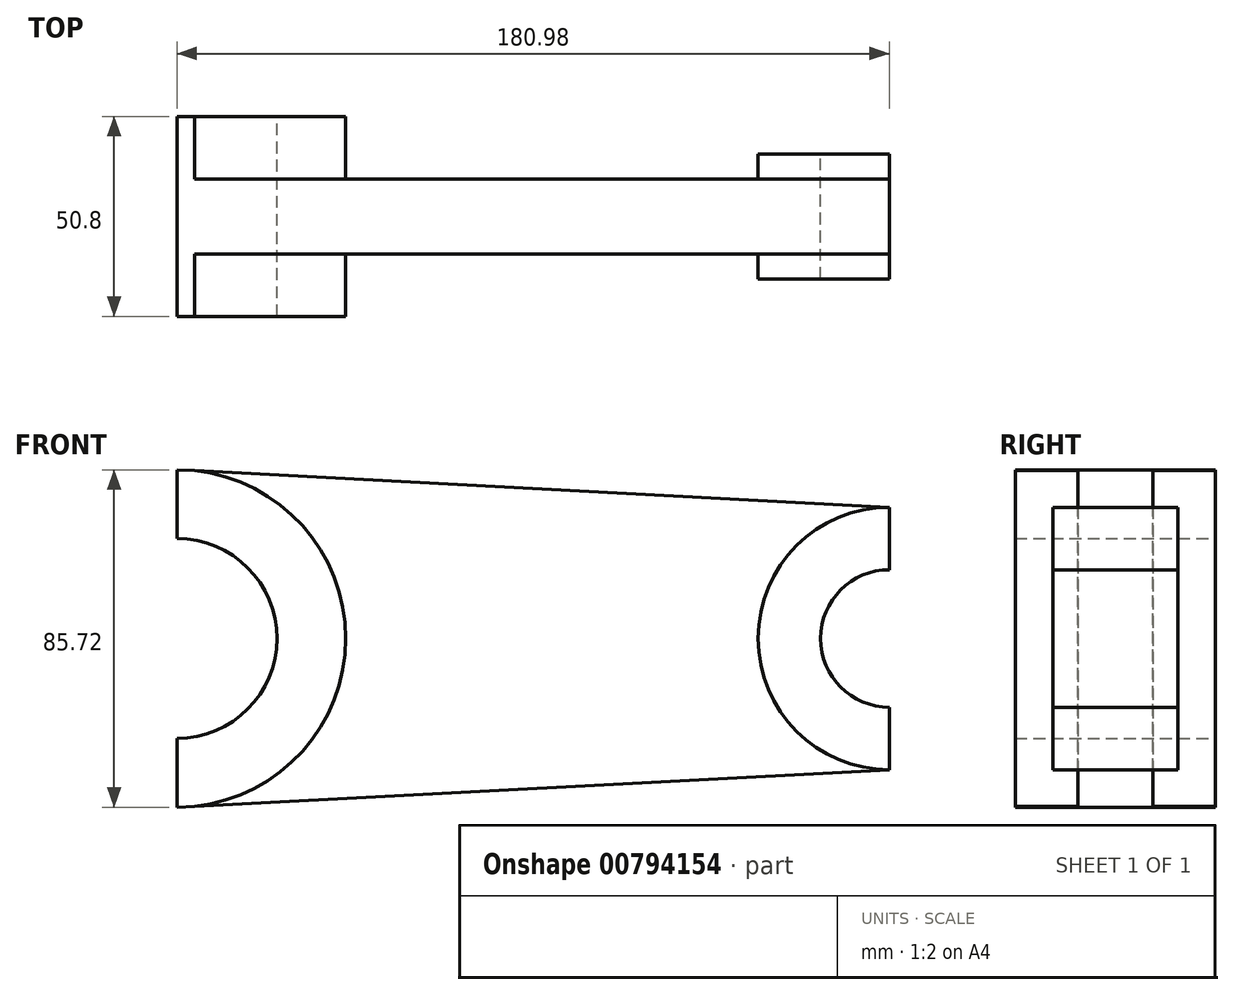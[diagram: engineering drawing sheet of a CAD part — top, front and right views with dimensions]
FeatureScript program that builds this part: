
annotation { "Feature Type Name" : "Feature", "Feature Type Description" : "" }
export const myFeature = defineFeature(function(context is Context, id is Id, definition is map)
    precondition{}
    {
        {
            var Q0;
            Q0=qCreatedBy(makeId("Front.planeOp"),FACE);
            var sketch = newSketch(context, id + "F0", { "sketchPlane" : qUnion([Q0])});
            skCircle(sketch, "E0", {"center": v(0, 0) * mm, "radius": 42.86 * mm});
            skCircle(sketch, "E1", {"center": v(0, 0) * mm, "radius": 25.4 * mm});
            skLineSegment(sketch, "E2", {"start": v(0, 0) * mm, "end": v(180.98, 0) * mm});
            skCircle(sketch, "E3", {"center": v(180.98, 0) * mm, "radius": 33.34 * mm});
            skCircle(sketch, "E4", {"center": v(180.98, 0) * mm, "radius": 17.46 * mm});
            skLineSegment(sketch, "E5", {"start": v(0, 0) * mm, "end": v(0, 42.86) * mm});
            skLineSegment(sketch, "E6", {"start": v(0, 42.86) * mm, "end": v(0, -42.86) * mm});
            skLineSegment(sketch, "E7", {"start": v(180.98, 0) * mm, "end": v(180.98, 33.34) * mm});
            skLineSegment(sketch, "E8", {"start": v(180.98, 33.34) * mm, "end": v(180.98, -33.34) * mm});
            skLineSegment(sketch, "E9", {"start": v(180.97, 33.34) * mm, "end": v(0, 42.86) * mm});
            skLineSegment(sketch, "E10", {"start": v(0, -42.86) * mm, "end": v(180.97, -33.34) * mm});
            skSolve(sketch);
        }
        {
            var Q0;
            {var subQ0=sQuery(id+"F0.wireOp",EDGE,"E9");var subQ2=sQuery(id+"F0.wireOp",EDGE,"E0");var subQ9=makeQuery(id+"F0.imprint","INTERSECT",VERTEX,{"derivedFrom":[subQ2,subQ0]});Q0=makeQuery(id+"F0.imprint","IMPRINT",FACE,{"disambiguationData":[TD([[makeQuery(id+"F0.imprint","IMPRINT",EDGE,{"disambiguationData":[TD([[subQ9,1.0]])],"derivedFrom":subQ2}),1.0]])]});}
            var Q1;
            {var subQ0=sQuery(id+"F0.wireOp",EDGE,"E6");var subQ4=sQuery(id+"F0.wireOp",EDGE,"E1");var subQ6=makeQuery(id+"F0.imprint","INTERSECT",VERTEX,{"disambiguationData":[OD(0.0)],"derivedFrom":[subQ4,subQ0]});Q1=makeQuery(id+"F0.imprint","IMPRINT",FACE,{"disambiguationData":[TD([[makeQuery(id+"F0.imprint","IMPRINT",EDGE,{"disambiguationData":[TD([[subQ6,-1.0]])],"derivedFrom":subQ4}),-1.0]])]});}
            var Q2;
            {var subQ0=sQuery(id+"F0.wireOp",EDGE,"E10");var subQ2=sQuery(id+"F0.wireOp",EDGE,"E0");var subQ8=makeQuery(id+"F0.imprint","INTERSECT",VERTEX,{"derivedFrom":[subQ2,subQ0]});Q2=makeQuery(id+"F0.imprint","IMPRINT",FACE,{"disambiguationData":[TD([[makeQuery(id+"F0.imprint","IMPRINT",EDGE,{"disambiguationData":[TD([[subQ8,-1.0]])],"derivedFrom":subQ2}),1.0]])]});}
            extrude(context, id + "F1", {"entities" : qUnion([Q0, Q1, Q2]), "depth" : 25.4 * mm, "offsetDistance" : 25.4 * mm});
        }
        {
            var Q0;
            Q0=makeQuery(id+"F1.opExtrude","CAP_FACE",FACE,{"disambiguationData":[OSD([sQuery(id+"F0.wireOp",EDGE,"E0"),sQuery(id+"F0.wireOp",EDGE,"E1"),sQuery(id+"F0.wireOp",EDGE,"E9"),sQuery(id+"F0.wireOp",EDGE,"E10")])],"isStart":true});
            extrude(context, id + "F2", {"entities" : qUnion([Q0]), "operationType" : NewBodyOperationType.ADD, "depth" : 25.4 * mm, "offsetDistance" : 25.4 * mm});
        }
        {
            var Q0;
            {var subQ0=sQuery(id+"F0.wireOp",EDGE,"E9");var subQ1=sQuery(id+"F0.wireOp",EDGE,"E0");var subQ2=makeQuery(id+"F0.imprint","INTERSECT",VERTEX,{"derivedFrom":[subQ1,subQ0]});Q0=makeQuery(id+"F0.imprint","IMPRINT",FACE,{"disambiguationData":[TD([[makeQuery(id+"F0.imprint","IMPRINT",EDGE,{"disambiguationData":[TD([[subQ2,1.0]])],"derivedFrom":subQ1}),-1.0]])]});}
            var Q1;
            {var subQ0=sQuery(id+"F0.wireOp",EDGE,"E10");var subQ1=sQuery(id+"F0.wireOp",EDGE,"E0");var subQ2=makeQuery(id+"F0.imprint","INTERSECT",VERTEX,{"derivedFrom":[subQ1,subQ0]});Q1=makeQuery(id+"F0.imprint","IMPRINT",FACE,{"disambiguationData":[TD([[makeQuery(id+"F0.imprint","IMPRINT",EDGE,{"disambiguationData":[TD([[subQ2,-1.0]])],"derivedFrom":subQ1}),-1.0]])]});}
            extrude(context, id + "F3", {"entities" : qUnion([Q0, Q1]), "operationType" : NewBodyOperationType.ADD, "depth" : 9.52 * mm, "offsetDistance" : 25.4 * mm});
        }
        {
            var Q0;
            {var subQ0=sQuery(id+"F0.wireOp",EDGE,"E10");var subQ1=sQuery(id+"F0.wireOp",EDGE,"E0");var subQ2=makeQuery(id+"F0.imprint","INTERSECT",VERTEX,{"derivedFrom":[subQ1,subQ0]});Q0=makeQuery(id+"F0.imprint","IMPRINT",FACE,{"disambiguationData":[TD([[makeQuery(id+"F0.imprint","IMPRINT",EDGE,{"disambiguationData":[TD([[subQ2,-1.0]])],"derivedFrom":subQ1}),-1.0]])]});}
            var Q1;
            {var subQ0=sQuery(id+"F0.wireOp",EDGE,"E9");var subQ1=sQuery(id+"F0.wireOp",EDGE,"E0");var subQ2=makeQuery(id+"F0.imprint","INTERSECT",VERTEX,{"derivedFrom":[subQ1,subQ0]});Q1=makeQuery(id+"F0.imprint","IMPRINT",FACE,{"disambiguationData":[TD([[makeQuery(id+"F0.imprint","IMPRINT",EDGE,{"disambiguationData":[TD([[subQ2,1.0]])],"derivedFrom":subQ1}),-1.0]])]});}
            extrude(context, id + "F4", {"entities" : qUnion([Q0, Q1]), "operationType" : NewBodyOperationType.ADD, "depth" : -9.52 * mm, "offsetDistance" : 25.4 * mm});
        }
        {
            var Q0;
            {var subQ0=sQuery(id+"F0.wireOp",EDGE,"E3");var subQ1=sQuery(id+"F0.wireOp",EDGE,"E2");var subQ2=makeQuery(id+"F0.imprint","INTERSECT",VERTEX,{"derivedFrom":[subQ1,subQ0]});Q0=makeQuery(id+"F0.imprint","IMPRINT",FACE,{"disambiguationData":[TD([[makeQuery(id+"F0.imprint","IMPRINT",EDGE,{"disambiguationData":[TD([[subQ2,-1.0]])],"derivedFrom":subQ1}),-1.0]])]});}
            var Q1;
            {var subQ0=sQuery(id+"F0.wireOp",EDGE,"E3");var subQ1=sQuery(id+"F0.wireOp",EDGE,"E2");var subQ2=makeQuery(id+"F0.imprint","INTERSECT",VERTEX,{"derivedFrom":[subQ1,subQ0]});Q1=makeQuery(id+"F0.imprint","IMPRINT",FACE,{"disambiguationData":[TD([[makeQuery(id+"F0.imprint","IMPRINT",EDGE,{"disambiguationData":[TD([[subQ2,-1.0]])],"derivedFrom":subQ1}),1.0]])]});}
            var Q2;
            {var subQ0=sQuery(id+"F0.wireOp",EDGE,"E8");var subQ4=sQuery(id+"F0.wireOp",EDGE,"E4");var subQ5=makeQuery(id+"F0.imprint","INTERSECT",VERTEX,{"disambiguationData":[OD(0.0)],"derivedFrom":[subQ4,subQ0]});Q2=makeQuery(id+"F0.imprint","IMPRINT",FACE,{"disambiguationData":[TD([[makeQuery(id+"F0.imprint","IMPRINT",EDGE,{"disambiguationData":[TD([[subQ5,1.0]])],"derivedFrom":subQ4}),-1.0]])]});}
            extrude(context, id + "F5", {"entities" : qUnion([Q0, Q1, Q2]), "operationType" : NewBodyOperationType.ADD, "depth" : 15.88 * mm, "offsetDistance" : 25.4 * mm});
        }
        {
            var Q0;
            {var subQ0=sQuery(id+"F0.wireOp",EDGE,"E3");var subQ1=sQuery(id+"F0.wireOp",EDGE,"E2");var subQ2=makeQuery(id+"F0.imprint","INTERSECT",VERTEX,{"derivedFrom":[subQ1,subQ0]});Q0=makeQuery(id+"F0.imprint","IMPRINT",FACE,{"disambiguationData":[TD([[makeQuery(id+"F0.imprint","IMPRINT",EDGE,{"disambiguationData":[TD([[subQ2,-1.0]])],"derivedFrom":subQ1}),-1.0]])]});}
            var Q1;
            {var subQ0=sQuery(id+"F0.wireOp",EDGE,"E3");var subQ1=sQuery(id+"F0.wireOp",EDGE,"E2");var subQ2=makeQuery(id+"F0.imprint","INTERSECT",VERTEX,{"derivedFrom":[subQ1,subQ0]});Q1=makeQuery(id+"F0.imprint","IMPRINT",FACE,{"disambiguationData":[TD([[makeQuery(id+"F0.imprint","IMPRINT",EDGE,{"disambiguationData":[TD([[subQ2,-1.0]])],"derivedFrom":subQ1}),1.0]])]});}
            var Q2;
            {var subQ0=sQuery(id+"F0.wireOp",EDGE,"E8");var subQ4=sQuery(id+"F0.wireOp",EDGE,"E4");var subQ5=makeQuery(id+"F0.imprint","INTERSECT",VERTEX,{"disambiguationData":[OD(0.0)],"derivedFrom":[subQ4,subQ0]});Q2=makeQuery(id+"F0.imprint","IMPRINT",FACE,{"disambiguationData":[TD([[makeQuery(id+"F0.imprint","IMPRINT",EDGE,{"disambiguationData":[TD([[subQ5,1.0]])],"derivedFrom":subQ4}),-1.0]])]});}
            extrude(context, id + "F6", {"entities" : qUnion([Q0, Q1, Q2]), "operationType" : NewBodyOperationType.ADD, "depth" : -15.88 * mm, "offsetDistance" : 25.4 * mm});
        }
    });
